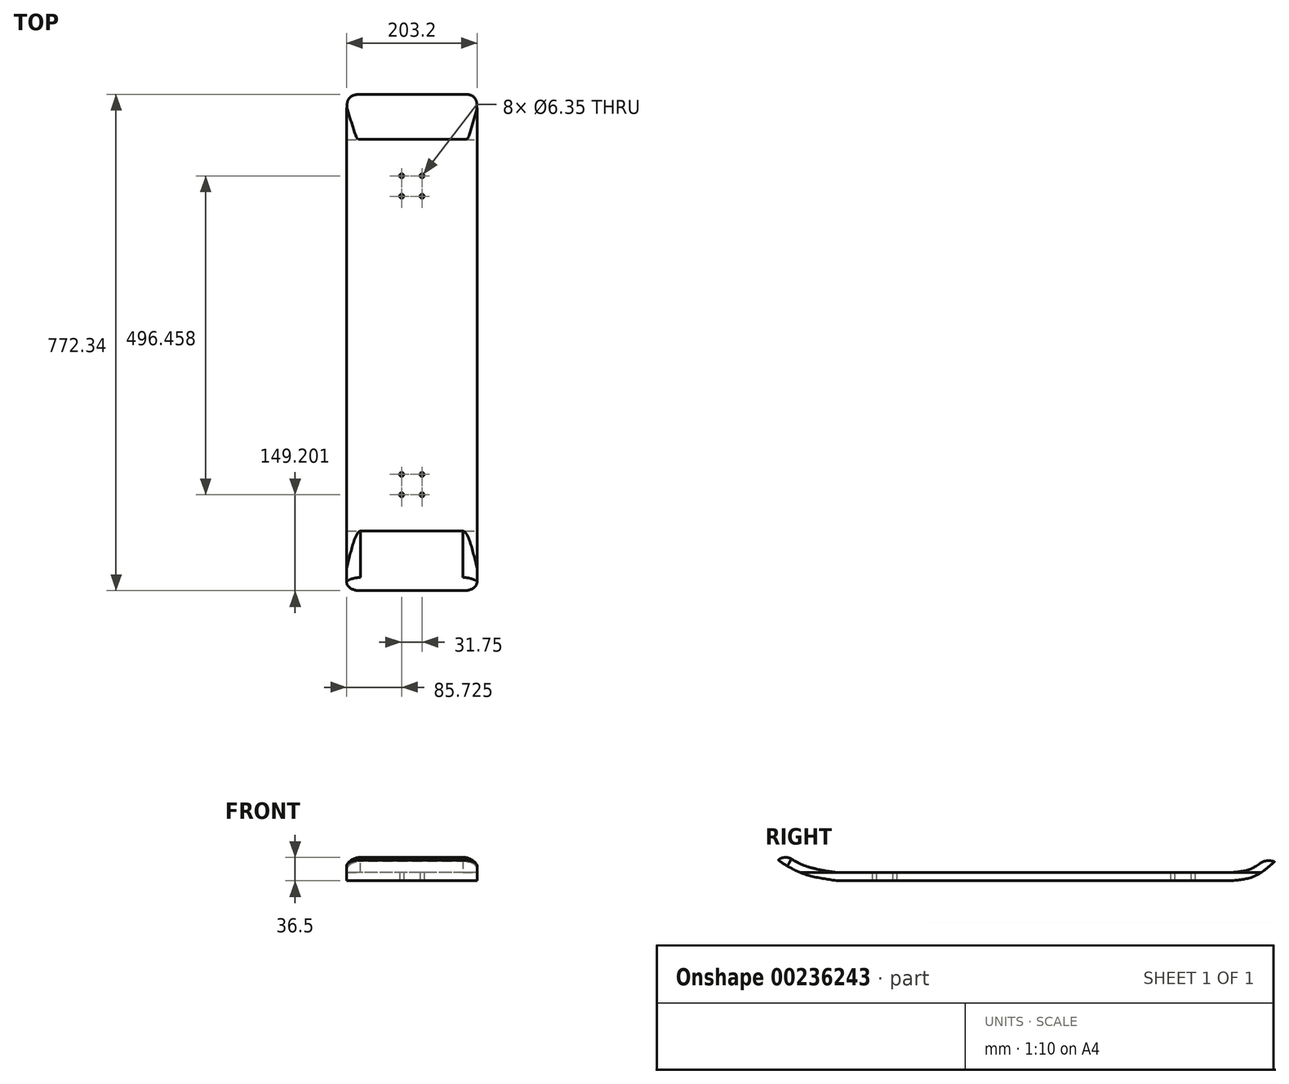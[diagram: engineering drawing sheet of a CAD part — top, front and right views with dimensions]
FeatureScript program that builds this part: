
annotation { "Feature Type Name" : "Feature", "Feature Type Description" : "" }
export const myFeature = defineFeature(function(context is Context, id is Id, definition is map)
    precondition{}
    {
        {
            var Q0;
            Q0=qCreatedBy(makeId("Top.planeOp"),FACE);
            var sketch = newSketch(context, id + "F0", { "sketchPlane" : qUnion([Q0])});
            skLineSegment(sketch, "E0.bottom", {"start": v(101.6, 304.8) * mm, "end": v(-101.6, 304.8) * mm});
            skLineSegment(sketch, "E0.top", {"start": v(101.6, -304.8) * mm, "end": v(-101.6, -304.8) * mm});
            skLineSegment(sketch, "E0.left", {"start": v(101.6, 304.8) * mm, "end": v(101.6, -304.8) * mm});
            skLineSegment(sketch, "E0.right", {"start": v(-101.6, 304.8) * mm, "end": v(-101.6, -304.8) * mm});
            skPoint(sketch, "E0.middle", {"position": v(0, 0) * mm});
            skPoint(sketch, "E1.middle", {"position": v(0, 232.35) * mm});
            skCircle(sketch, "E2", {"center": v(-15.88, 248.23) * mm, "radius": 3.18 * mm});
            skCircle(sketch, "E3", {"center": v(15.88, 248.23) * mm, "radius": 3.18 * mm});
            skCircle(sketch, "E4", {"center": v(-15.88, 216.48) * mm, "radius": 3.18 * mm});
            skCircle(sketch, "E5", {"center": v(15.88, 216.48) * mm, "radius": 3.18 * mm});
            skPoint(sketch, "E1.right.end.orphan", {"position": v(-25.4, 257.75) * mm});
            skPoint(sketch, "E1.bottom.end.orphan", {"position": v(-25.4, 206.95) * mm});
            skPoint(sketch, "E1.left.end.orphan", {"position": v(25.4, 257.75) * mm});
            skPoint(sketch, "E1.left.start.orphan", {"position": v(25.4, 206.95) * mm});
            skCircle(sketch, "E6.MirrorC", {"center": v(15.88, -216.48) * mm, "radius": 3.18 * mm});
            skCircle(sketch, "E7.MirrorC", {"center": v(-15.88, -216.48) * mm, "radius": 3.18 * mm});
            skCircle(sketch, "E8.MirrorC", {"center": v(-15.88, -248.23) * mm, "radius": 3.18 * mm});
            skCircle(sketch, "E9.MirrorC", {"center": v(15.88, -248.23) * mm, "radius": 3.18 * mm});
            skPoint(sketch, "E10.MirrorP", {"position": v(25.4, -206.95) * mm});
            skPoint(sketch, "E11.MirrorP", {"position": v(25.4, -257.75) * mm});
            skPoint(sketch, "E12.MirrorP", {"position": v(-25.4, -206.95) * mm});
            skPoint(sketch, "E13.MirrorP", {"position": v(-25.4, -257.75) * mm});
            skSolve(sketch);
        }
        {
            var Q0;
            Q0 = qSketchRegion(id + "F0", true);
            extrude(context, id + "F1", {"entities" : qUnion([Q0]), "endBound" : BoundingType.SYMMETRIC, "depth" : 12.7 * mm});
        }
        {
            var Q0;
            Q0=qCreatedBy(makeId("Right.planeOp"),FACE);
            var sketch = newSketch(context, id + "F2", { "sketchPlane" : qUnion([Q0])});
            skFitSpline(sketch, "E14", {"points": [v(304.63, 0) * mm, v(340.78, 6.52) * mm, v(371, 28.45) * mm], "startDerivative": vector(75.69, 5.48) * mm, "endDerivative": vector(57.1, 51.36) * mm});
            skFitSpline(sketch, "E15", {"points": [v(-304.61, 0) * mm, v(-358.15, 11.24) * mm, v(-395.82, 32.39) * mm], "startDerivative": vector(-106.69, 14.94) * mm, "endDerivative": vector(-75.11, 50.53) * mm});
            skSolve(sketch);
        }
        {
            var Q0;
            Q0=makeQuery(id+"F1.opExtrude","SWEPT_FACE",FACE,{"disambiguationData":[OSD([sQuery(id+"F0.wireOp",EDGE,"E0.bottom")])]});
            var Q1;
            Q1=sQuery(id+"F2.wireOp",EDGE,"E14");
            sweep(context, id + "F3", {"operationType" : NewBodyOperationType.ADD, "profiles" : qUnion([Q0]), "path" : qUnion([Q1])});
        }
        {
            var Q0;
            Q0=makeQuery(id+"F1.opExtrude","SWEPT_FACE",FACE,{"disambiguationData":[OSD([sQuery(id+"F0.wireOp",EDGE,"E0.top")])]});
            var Q1;
            Q1=sQuery(id+"F2.wireOp",EDGE,"E15");
            sweep(context, id + "F4", {"operationType" : NewBodyOperationType.ADD, "profiles" : qUnion([Q0]), "path" : qUnion([Q1])});
        }
        {
            var Q0;
            {var subQ0=sQuery(id+"F2.wireOp",EDGE,"E15");var subQ1=sQuery(id+"F0.wireOp",EDGE,"E0.left");var subQ2=sQuery(id+"F0.wireOp",EDGE,"E0.top");Q0=makeQuery(id+"F4.opSweep","SWEPT_EDGE",EDGE,{"disambiguationData":[OSD([subQ2,subQ1,subQ0]),TDD([makeQuery(id+"F1.opExtrude","CAP_VERTEX",VERTEX,{"disambiguationData":[OSD([subQ2,subQ1])],"isStart":false}),subQ0])]});}
            fillet(context, id + "F5", {"entities" : qUnion([Q0]), "radius" : 25.4 * mm, "tangentPropagation" : true, "allowEdgeOverflow" : false});
        }
        {
            var Q0;
            {var subQ0=sQuery(id+"F2.wireOp",EDGE,"E15");var subQ1=sQuery(id+"F0.wireOp",EDGE,"E0.right");var subQ2=sQuery(id+"F0.wireOp",EDGE,"E0.top");Q0=makeQuery(id+"F4.opSweep","SWEPT_EDGE",EDGE,{"disambiguationData":[OSD([subQ2,subQ1,subQ0]),TDD([makeQuery(id+"F1.opExtrude","CAP_VERTEX",VERTEX,{"disambiguationData":[OSD([subQ2,subQ1])],"isStart":false}),subQ0])]});}
            fillet(context, id + "F6", {"entities" : qUnion([Q0]), "radius" : 25.4 * mm, "tangentPropagation" : true, "allowEdgeOverflow" : false});
        }
        {
            var Q0;
            {var subQ0=sQuery(id+"F2.wireOp",VERTEX,"E15.end");var subQ1=sQuery(id+"F0.wireOp",EDGE,"E0.top");Q0=makeQuery(id+"F4.opSweep","CAP_EDGE",EDGE,{"disambiguationData":[OSD([subQ1,subQ0]),TDD([makeQuery(id+"F1.opExtrude","CAP_EDGE",EDGE,{"disambiguationData":[OSD([subQ1])],"isStart":false}),subQ0])],"isStart":false});}
            fillet(context, id + "F7", {"entities" : qUnion([Q0]), "radius" : 17.46 * mm, "tangentPropagation" : true, "allowEdgeOverflow" : false});
        }
        {
            var Q0;
            {var subQ0=sQuery(id+"F2.wireOp",VERTEX,"E14.end");var subQ1=sQuery(id+"F0.wireOp",EDGE,"E0.bottom");Q0=makeQuery(id+"F3.opSweep","CAP_EDGE",EDGE,{"disambiguationData":[OSD([subQ1,subQ0]),TDD([makeQuery(id+"F1.opExtrude","CAP_EDGE",EDGE,{"disambiguationData":[OSD([subQ1])],"isStart":false}),subQ0])],"isStart":false});}
            fillet(context, id + "F8", {"entities" : qUnion([Q0]), "radius" : 25.4 * mm, "tangentPropagation" : true, "allowEdgeOverflow" : false});
        }
        {
            var Q0;
            {var subQ0=sQuery(id+"F2.wireOp",EDGE,"E14");var subQ1=sQuery(id+"F0.wireOp",EDGE,"E0.right");var subQ2=sQuery(id+"F0.wireOp",EDGE,"E0.bottom");Q0=makeQuery(id+"F3.opSweep","SWEPT_EDGE",EDGE,{"disambiguationData":[OSD([subQ2,subQ1,subQ0]),TDD([makeQuery(id+"F1.opExtrude","CAP_VERTEX",VERTEX,{"disambiguationData":[OSD([subQ2,subQ1])],"isStart":false}),subQ0])]});}
            fillet(context, id + "F9", {"entities" : qUnion([Q0]), "radius" : 18.4 * mm, "tangentPropagation" : true, "allowEdgeOverflow" : false});
        }
        {
            var Q0;
            {var subQ0=sQuery(id+"F2.wireOp",EDGE,"E14");var subQ1=sQuery(id+"F0.wireOp",EDGE,"E0.left");var subQ2=sQuery(id+"F0.wireOp",EDGE,"E0.bottom");Q0=makeQuery(id+"F3.opSweep","SWEPT_EDGE",EDGE,{"disambiguationData":[OSD([subQ2,subQ1,subQ0]),TDD([makeQuery(id+"F1.opExtrude","CAP_VERTEX",VERTEX,{"disambiguationData":[OSD([subQ2,subQ1])],"isStart":false}),subQ0])]});}
            fillet(context, id + "F10", {"entities" : qUnion([Q0]), "radius" : 16.56 * mm, "tangentPropagation" : true, "allowEdgeOverflow" : false});
        }
    });
